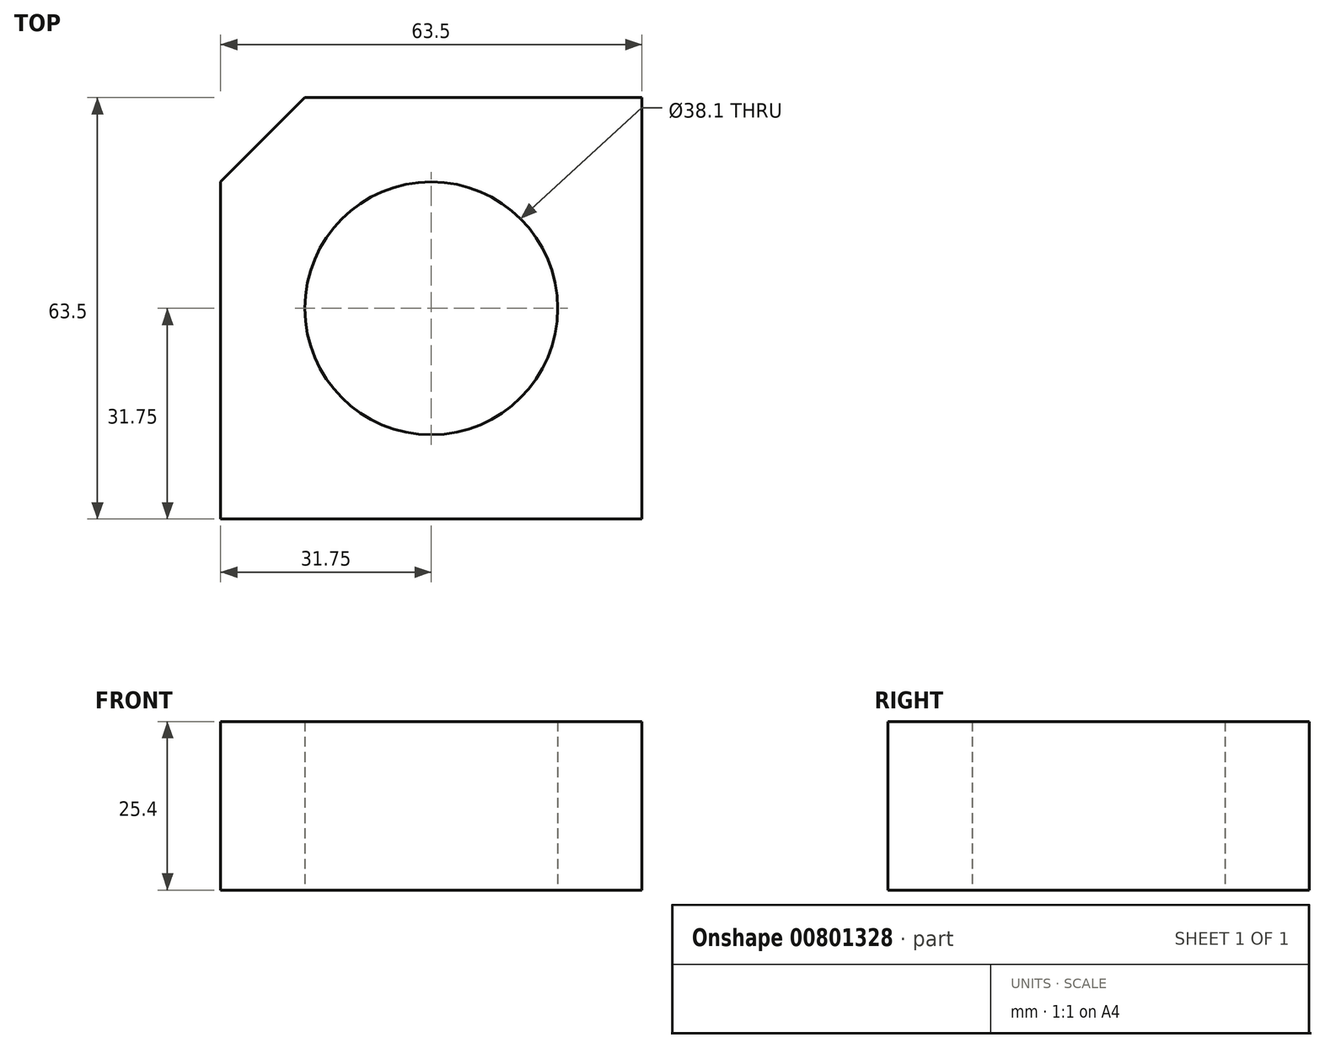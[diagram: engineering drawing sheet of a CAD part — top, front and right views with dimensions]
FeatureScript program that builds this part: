
annotation { "Feature Type Name" : "Feature", "Feature Type Description" : "" }
export const myFeature = defineFeature(function(context is Context, id is Id, definition is map)
    precondition{}
    {
        {
            var Q0;
            Q0=qCreatedBy(makeId("Top.planeOp"),FACE);
            var sketch = newSketch(context, id + "F0", { "sketchPlane" : qUnion([Q0])});
            skLineSegment(sketch, "E0.bottom", {"start": v(0, 0) * mm, "end": v(-63.5, 0) * mm});
            skLineSegment(sketch, "E0.top", {"start": v(0, 63.5) * mm, "end": v(-63.5, 63.5) * mm});
            skLineSegment(sketch, "E0.left", {"start": v(0, 0) * mm, "end": v(0, 63.5) * mm});
            skLineSegment(sketch, "E0.right", {"start": v(-63.5, 0) * mm, "end": v(-63.5, 63.5) * mm});
            skCircle(sketch, "E1", {"center": v(-31.75, 31.75) * mm, "radius": 19.05 * mm});
            skPoint(sketch, "E1.centerSnap0", {"position": v(-63.5, 31.75) * mm});
            skPoint(sketch, "E1.centerSnap1", {"position": v(-31.75, 0) * mm});
            skLineSegment(sketch, "E2", {"start": v(-63.5, 50.8) * mm, "end": v(-50.8, 63.5) * mm});
            skSolve(sketch);
        }
        {
            var Q0;
            {var subQ1=sQuery(id+"F0.wireOp",EDGE,"E0.bottom");Q0=makeQuery(id+"F0.imprint","IMPRINT",FACE,{"disambiguationData":[TD([[makeQuery(id+"F0.imprint","IMPRINT",EDGE,{"derivedFrom":subQ1}),-1.0]])]});}
            extrude(context, id + "F1", {"entities" : qUnion([Q0]), "depth" : 25.4 * mm, "offsetDistance" : 25.4 * mm});
        }
    });
